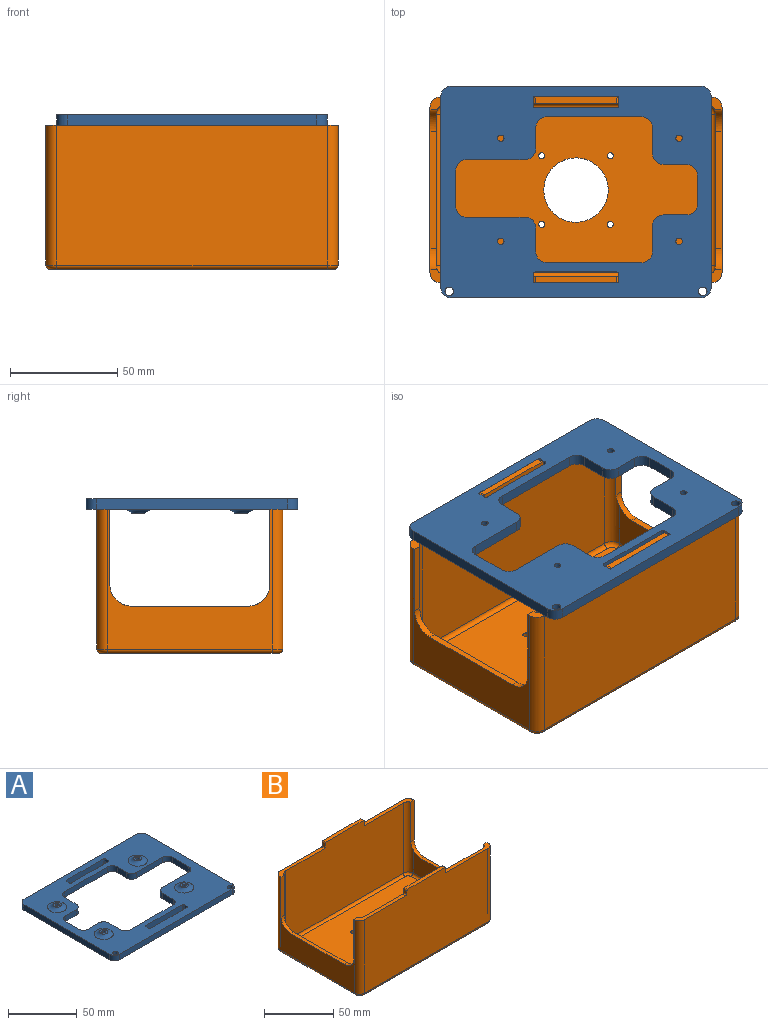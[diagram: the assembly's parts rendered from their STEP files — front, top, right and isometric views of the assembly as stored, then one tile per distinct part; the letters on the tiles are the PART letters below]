
ASSEMBLY  parts=2 mates=1
PART A: 64 faces, bbox 126x98.5x10 mm
  f0: plane 126x98.5mm, normal (0,0,1), area 6190.5mm2, adj f2,f3,f4,f5,f6,f7,f8,f9
  f1: plane 126x98.5mm, normal (0,0,-1), area 6778mm2, adj f2,f3,f4,f5,f6,f7,f8,f9
  f2: plane 5x3mm, normal (-1,0,0), area 15mm2, adj f0,f1,f22,f25
  f3: plane 38x5mm, normal (0,1,0), area 190mm2, adj f0,f1,f22,f23
  f4: plane 5x3mm, normal (1,0,0), area 15mm2, adj f0,f1,f23,f24
  f5: plane 116x5mm, normal (0,1,0), area 580mm2, adj f0,f1,f28,f29
  f6: plane 88.5x5mm, normal (-1,0,0), area 442.5mm2, adj f0,f1,f28,f30
  f7: plane 116x5mm, normal (0,-1,0), area 580mm2, adj f0,f1,f30,f31
  f8: plane 5x3mm, normal (1,0,0), area 15mm2, adj f0,f1,f20,f27
  f9: plane 38x5mm, normal (0,-1,0), area 190mm2, adj f0,f1,f20,f21
  f10: plane 5x3mm, normal (-1,0,0), area 15mm2, adj f0,f1,f21,f26
  f11: cylinder r=1.5mm len=7mm, axis (0,0,-1), area 66mm2, adj f1,f33
  f12: cylinder r=1.5mm len=7mm, axis (0,0,-1), area 66mm2, adj f1,f34
  f13: cylinder r=1.5mm len=7mm, axis (0,0,-1), area 66mm2, adj f1,f35
  f14: plane 38x5mm, normal (0,-1,0), area 190mm2, adj f0,f1,f24,f25
  f15: cylinder r=2mm len=5mm, axis (0,0,-1), area 62.8mm2, adj f0,f1
  f16: cylinder r=2mm len=5mm, axis (0,0,-1), area 62.8mm2, adj f0,f1
  f17: plane 88.5x5mm, normal (1,0,0), area 442.5mm2, adj f0,f1,f29,f31
  f18: plane 38x5mm, normal (0,1,0), area 190mm2, adj f0,f1,f26,f27
  f19: cylinder r=1.5mm len=7mm, axis (0,0,-1), area 66mm2, adj f1,f32
  f20: cylinder r=1mm len=5mm, axis (0,0,-1), area 7.9mm2, adj f0,f1,f8,f9
  f21: cylinder r=1mm len=5mm, axis (0,0,1), area 7.9mm2, adj f0,f1,f9,f10
  f22: cylinder r=1mm len=5mm, axis (0,0,1), area 7.9mm2, adj f0,f1,f2,f3
  f23: cylinder r=1mm len=5mm, axis (0,0,-1), area 7.9mm2, adj f0,f1,f3,f4
  f24: cylinder r=1mm len=5mm, axis (0,0,1), area 7.9mm2, adj f0,f1,f4,f14
  f25: cylinder r=1mm len=5mm, axis (0,0,-1), area 7.9mm2, adj f0,f1,f2,f14
  f26: cylinder r=1mm len=5mm, axis (0,0,-1), area 7.9mm2, adj f0,f1,f10,f18
  f27: cylinder r=1mm len=5mm, axis (0,0,1), area 7.9mm2, adj f0,f1,f8,f18
  f28: cylinder r=5mm len=5mm, axis (0,0,1), area 39.3mm2, adj f0,f1,f5,f6
  f29: cylinder r=5mm len=5mm, axis (0,0,-1), area 39.3mm2, adj f0,f1,f5,f17
  f30: cylinder r=5mm len=5mm, axis (0,0,-1), area 39.3mm2, adj f0,f1,f6,f7
  f31: cylinder r=5mm len=5mm, axis (0,0,1), area 39.3mm2, adj f0,f1,f7,f17
  f32: plane 6x6mm, normal (0,0,1), area 21.2mm2, adj f19,f39
  f33: plane 6x6mm, normal (0,0,1), area 21.2mm2, adj f11,f38
  f34: plane 6x6mm, normal (0,0,1), area 21.2mm2, adj f12,f37
  f35: plane 6x6mm, normal (0,0,1), area 21.2mm2, adj f13,f36
  f36: torus R=7mm, axis (0,0,1), area 141.1mm2, adj f0,f35
  f37: torus R=7mm, axis (0,0,1), area 141.1mm2, adj f0,f34
  f38: torus R=7mm, axis (0,0,1), area 141.1mm2, adj f0,f33
  f39: torus R=7mm, axis (0,0,1), area 141.1mm2, adj f0,f32
  f40: plane 10.92x5mm, normal (0,-1,0), area 54.6mm2, adj f0,f1,f52,f55
  f41: plane 13.53x5mm, normal (1,0,0), area 67.7mm2, adj f0,f1,f52,f53
  f42: plane 10.92x5mm, normal (0,1,0), area 54.6mm2, adj f0,f1,f53,f54
  f43: plane 12.23x5mm, normal (1,0,0), area 61.2mm2, adj f0,f1,f54,f61
  f44: plane 44.32x5mm, normal (0,1,0), area 221.6mm2, adj f0,f1,f61,f62
  f45: plane 11.15x5mm, normal (-1,0,0), area 55.7mm2, adj f0,f1,f57,f62
  f46: plane 27.23x5mm, normal (0,1,0), area 136.2mm2, adj f0,f1,f57,f58
  f47: plane 16.9x5mm, normal (-1,0,0), area 84.5mm2, adj f0,f1,f58,f59
  f48: plane 27.23x5mm, normal (0,-1,0), area 136.2mm2, adj f0,f1,f56,f59
  f49: plane 9.84x5mm, normal (-1,0,0), area 49.2mm2, adj f0,f1,f56,f63
  f50: plane 44.32x5mm, normal (0,-1,0), area 221.6mm2, adj f0,f1,f60,f63
  f51: plane 12.12x5mm, normal (1,0,0), area 60.6mm2, adj f0,f1,f55,f60
  f52: cylinder r=5mm len=5mm, axis (0,0,1), area 39.3mm2, adj f0,f1,f40,f41
  f53: cylinder r=5mm len=5mm, axis (0,0,-1), area 39.3mm2, adj f0,f1,f41,f42
  f54: cylinder r=5mm len=5mm, axis (0,0,1), area 39.3mm2, adj f0,f1,f42,f43
  f55: cylinder r=5mm len=5mm, axis (0,0,-1), area 39.3mm2, adj f0,f1,f40,f51
  f56: cylinder r=5mm len=5mm, axis (0,0,1), area 39.3mm2, adj f0,f1,f48,f49
  f57: cylinder r=5mm len=5mm, axis (0,0,-1), area 39.3mm2, adj f0,f1,f45,f46
  f58: cylinder r=5mm len=5mm, axis (0,0,1), area 39.3mm2, adj f0,f1,f46,f47
  f59: cylinder r=5mm len=5mm, axis (0,0,-1), area 39.3mm2, adj f0,f1,f47,f48
  f60: cylinder r=5mm len=5mm, axis (0,0,1), area 39.3mm2, adj f0,f1,f50,f51
  f61: cylinder r=5mm len=5mm, axis (0,0,-1), area 39.3mm2, adj f0,f1,f43,f44
  f62: cylinder r=5mm len=5mm, axis (0,0,1), area 39.3mm2, adj f0,f1,f44,f45
  f63: cylinder r=5mm len=5mm, axis (0,0,-1), area 39.3mm2, adj f0,f1,f49,f50
PART B: 67 faces, bbox 136.8x87.3x72 mm
  f0: plane 47.1x6mm, normal (0,0,1), area 150mm2, adj f2,f14,f17,f28,f36,f43,f44
  f1: plane 47.1x6mm, normal (0,0,1), area 150mm2, adj f12,f15,f16,f19,f40,f47,f48
  f2: plane 76.5x65mm, normal (-1,0,0), area 1660.7mm2, adj f0,f3,f24,f25,f26,f27,f28,f44
  f3: plane 47.1x6mm, normal (0,0,1), area 150mm2, adj f2,f12,f15,f27,f39,f49,f50
  f4: cylinder r=1.4mm len=3mm, axis (0,0,-1), area 26.4mm2, adj f9,f10
  f5: cylinder r=1.4mm len=3mm, axis (0,0,-1), area 26.4mm2, adj f9,f10
  f6: cylinder r=1.4mm len=3mm, axis (0,0,-1), area 26.4mm2, adj f9,f10
  f7: cylinder r=1.4mm len=3mm, axis (0,0,-1), area 26.4mm2, adj f9,f10
  f8: cylinder r=15mm len=30mm, axis (0,0,-1), area 282.7mm2, adj f9,f10
  f9: plane 126x76.5mm, normal (0,0,1), area 8899.8mm2, adj f4,f5,f6,f7,f8,f59,f60,f61
  f10: plane 132x82.5mm, normal (0,0,-1), area 10150.8mm2, adj f4,f5,f6,f7,f8,f51,f52,f53
  f11: plane 70.5x20.97mm, normal (1,0,0), area 1215.7mm2, adj f24,f25,f26,f43,f49,f62
  f12: plane 120x67mm, normal (0,1,0), area 7639mm2, adj f1,f3,f29,f30,f31,f39,f40,f41
  f13: plane 70.5x20.97mm, normal (-1,0,0), area 1215.7mm2, adj f20,f21,f23,f45,f48,f63
  f14: plane 120x67mm, normal (0,-1,0), area 7639mm2, adj f0,f18,f32,f33,f34,f35,f36,f37
  f15: plane 126x70mm, normal (0,-1,0), area 8389mm2, adj f1,f3,f29,f30,f31,f39,f40,f41
  f16: plane 76.5x65mm, normal (1,0,0), area 1660.7mm2, adj f1,f18,f19,f20,f21,f22,f23,f46
  f17: plane 126x70mm, normal (0,1,0), area 8389mm2, adj f0,f18,f32,f33,f34,f35,f36,f37
  f18: plane 47.1x6mm, normal (0,0,1), area 150mm2, adj f14,f16,f17,f22,f35,f45,f46
  f19: plane 35.03x3.42mm, normal (0,1,0), area 119.7mm2, adj f1,f16,f23,f48
  f20: plane 54.5x3mm, normal (0,0,1), area 163.5mm2, adj f13,f16,f21,f23
  f21: cylinder r=10mm len=10mm, axis (-1,0,0), area 48.5mm2, adj f13,f16,f20,f22,f45
  f22: plane 35.03x3.42mm, normal (0,-1,0), area 119.7mm2, adj f16,f18,f21,f45
  f23: cylinder r=10mm len=10mm, axis (-1,0,0), area 48.5mm2, adj f13,f16,f19,f20,f48
  f24: cylinder r=10mm len=10mm, axis (-1,0,0), area 48.5mm2, adj f2,f11,f26,f27,f49
  f25: cylinder r=10mm len=10mm, axis (-1,0,0), area 48.5mm2, adj f2,f11,f26,f28,f43
  f26: plane 54.5x3mm, normal (0,0,1), area 163.5mm2, adj f2,f11,f24,f25
  f27: plane 35.03x3.42mm, normal (0,1,0), area 119.7mm2, adj f2,f3,f24,f49
  f28: plane 35.03x3.42mm, normal (0,-1,0), area 119.7mm2, adj f0,f2,f25,f43
  f29: plane 3x3mm, normal (1,0,0), area 9mm2, adj f12,f15,f40,f42
  f30: plane 3x3mm, normal (-1,0,0), area 9mm2, adj f12,f15,f39,f41
  f31: plane 37.8x3mm, normal (0,0,1), area 113.4mm2, adj f12,f15,f41,f42
  f32: plane 3x3mm, normal (-1,0,0), area 9mm2, adj f14,f17,f36,f38
  f33: plane 3x3mm, normal (1,0,0), area 9mm2, adj f14,f17,f35,f37
  f34: plane 37.8x3mm, normal (0,0,1), area 113.4mm2, adj f14,f17,f37,f38
  f35: cylinder r=1mm len=3mm, axis (0,1,0), area 4.7mm2, adj f14,f17,f18,f33
  f36: cylinder r=1mm len=3mm, axis (0,-1,0), area 4.7mm2, adj f0,f14,f17,f32
  f37: cylinder r=1mm len=3mm, axis (0,-1,0), area 4.7mm2, adj f14,f17,f33,f34
  f38: cylinder r=1mm len=3mm, axis (0,1,0), area 4.7mm2, adj f14,f17,f32,f34
  f39: cylinder r=1mm len=3mm, axis (0,-1,0), area 4.7mm2, adj f3,f12,f15,f30
  f40: cylinder r=1mm len=3mm, axis (0,1,0), area 4.7mm2, adj f1,f12,f15,f29
  f41: cylinder r=1mm len=3mm, axis (0,1,0), area 4.7mm2, adj f12,f15,f30,f31
  f42: cylinder r=1mm len=3mm, axis (0,-1,0), area 4.7mm2, adj f12,f15,f29,f31
  f43: cylinder r=5mm len=62mm, axis (0,0,1), area 406.5mm2, adj f0,f11,f14,f25,f28,f60
  f44: cylinder r=5mm len=65mm, axis (0,0,-1), area 510.5mm2, adj f0,f2,f17,f56
  f45: cylinder r=5mm len=62mm, axis (0,0,-1), area 406.5mm2, adj f13,f14,f18,f21,f22,f61
  f46: cylinder r=5mm len=65mm, axis (0,0,1), area 510.5mm2, adj f16,f17,f18,f57
  f47: cylinder r=5mm len=65mm, axis (0,0,-1), area 510.5mm2, adj f1,f15,f16,f53
  f48: cylinder r=5mm len=62mm, axis (0,0,1), area 406.5mm2, adj f1,f12,f13,f19,f23,f65
  f49: cylinder r=5mm len=62mm, axis (0,0,-1), area 406.5mm2, adj f3,f11,f12,f24,f27,f64
  f50: cylinder r=5mm len=65mm, axis (0,0,1), area 510.5mm2, adj f2,f3,f15,f52
  f51: cylinder r=2mm len=126mm, axis (1,0,0), area 395.8mm2, adj f10,f15,f52,f53
  f52: torus R=3mm, axis (0,0,1), area 21.1mm2, adj f10,f50,f51,f54
  f53: torus R=3mm, axis (0,0,1), area 21.1mm2, adj f10,f47,f51,f55
  f54: cylinder r=2mm len=76.5mm, axis (0,-1,0), area 240.3mm2, adj f2,f10,f52,f56
  f55: cylinder r=2mm len=76.5mm, axis (0,1,0), area 240.3mm2, adj f10,f16,f53,f57
  f56: torus R=3mm, axis (0,0,1), area 21.1mm2, adj f10,f44,f54,f58
  f57: torus R=3mm, axis (0,0,1), area 21.1mm2, adj f10,f46,f55,f58
  f58: cylinder r=2mm len=126mm, axis (-1,0,0), area 395.8mm2, adj f10,f17,f56,f57
  f59: cylinder r=2mm len=120mm, axis (1,0,0), area 377mm2, adj f9,f14,f60,f61
  f60: torus R=3mm, axis (0,0,1), area 21.1mm2, adj f9,f43,f59,f62
  f61: torus R=3mm, axis (0,0,1), area 21.1mm2, adj f9,f45,f59,f63
  f62: cylinder r=2mm len=70.5mm, axis (0,1,0), area 221.5mm2, adj f9,f11,f60,f64
  f63: cylinder r=2mm len=70.5mm, axis (0,-1,0), area 221.5mm2, adj f9,f13,f61,f65
  f64: torus R=3mm, axis (0,0,1), area 21.1mm2, adj f9,f49,f62,f66
  f65: torus R=3mm, axis (0,0,1), area 21.1mm2, adj f9,f48,f63,f66
  f66: cylinder r=2mm len=120mm, axis (-1,0,0), area 377mm2, adj f9,f12,f64,f65
PLACE A rot(axis=(0,1,0),180deg) t=(97.63,40.8,107.17)mm
PLACE B t=(79.76,43.8,35.17)mm
MATE fastened A.f1 <-> B.f31  axis (0,0,1) through (84.39,47.8,107.17)mm
